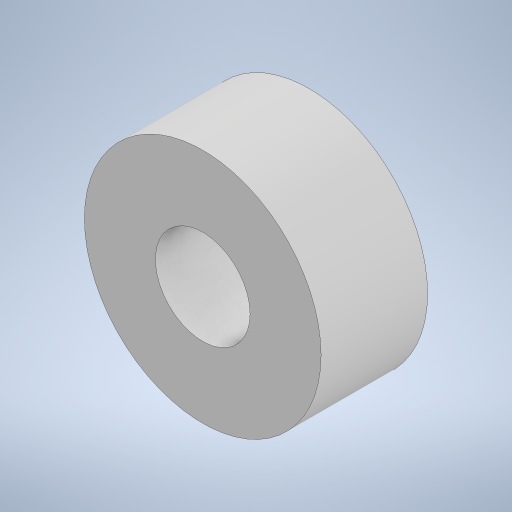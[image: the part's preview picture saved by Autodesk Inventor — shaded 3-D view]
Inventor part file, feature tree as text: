
AUTODESK INVENTOR PART (.ipt)
format: ipt  version: 2023 (Build 270158000, 158)  size: 208,384 bytes
history: native  units: in
note: dims shown in document units (in); Inventor stores cm internally (conversion verified against a paired STEP export)
features: extrude x1, sketch x1
ambient origin geometry x8: Origin, YZ Plane, XZ Plane, XY Plane, X Axis, Y Axis, Z Axis, Center Point
bodies: Solid1 (feature_tree)
feature tree (2):
  extrude  "Extrusion1"  Depth=0.2812in
  sketch  "Sketch1"  dims[d0=0.25in d1=0.625in d2=0.2812in d3=0.0in]
